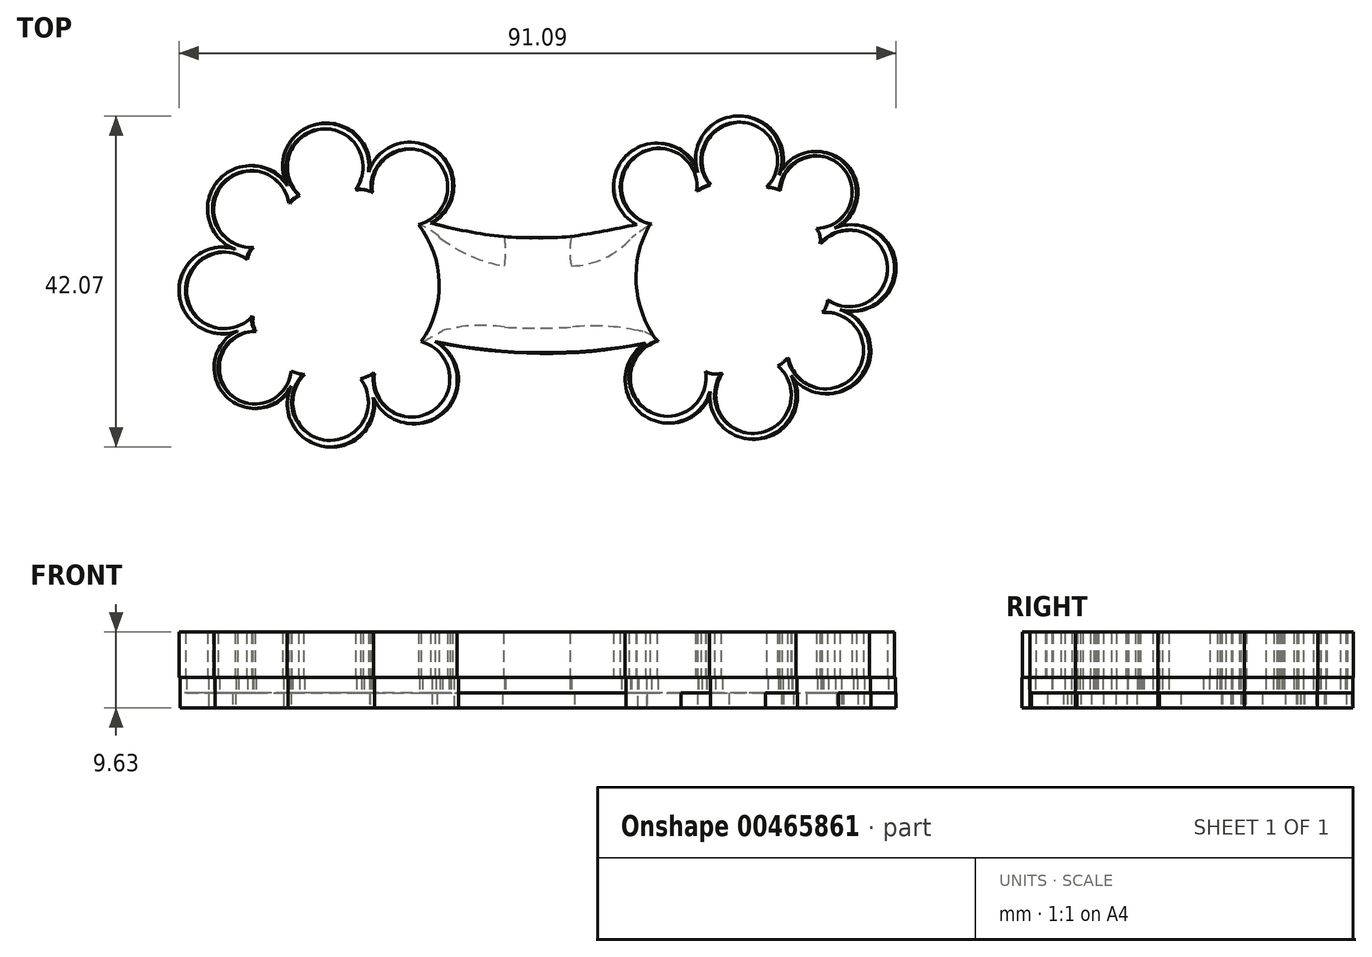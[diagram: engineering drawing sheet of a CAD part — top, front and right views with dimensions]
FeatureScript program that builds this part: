
annotation { "Feature Type Name" : "Feature", "Feature Type Description" : "" }
export const myFeature = defineFeature(function(context is Context, id is Id, definition is map)
    precondition{}
    {
        {
            var Q0;
            Q0=qCreatedBy(makeId("Top.planeOp"),FACE);
            var sketch = newSketch(context, id + "F0", { "sketchPlane" : qUnion([Q0])});
            skCircle(sketch, "E0", {"center": v(-25.13, 0.69) * mm, "radius": 13.9 * mm});
            skArc(sketch, "E1", {"start": v(-21.88, 14.2) * mm, "mid": v(-27.79, 21.36) * mm, "end": v(-31.7, 12.95) * mm});
            skArc(sketch, "E2", {"start": v(-31.7, 12.95) * mm, "mid": v(-40.8, 14.09) * mm, "end": v(-38.24, 5.29) * mm});
            skArc(sketch, "E3", {"start": v(-38.24, 5.29) * mm, "mid": v(-45.72, 0) * mm, "end": v(-37.92, -4.8) * mm});
            skArc(sketch, "E4", {"start": v(-13.74, 8.67) * mm, "mid": v(-13.36, 17.98) * mm, "end": v(-21.88, 14.2) * mm});
            skArc(sketch, "E5", {"start": v(-37.92, -4.8) * mm, "mid": v(-39.87, -13.17) * mm, "end": v(-31.4, -11.73) * mm});
            skArc(sketch, "E6", {"start": v(-31.4, -11.73) * mm, "mid": v(-27, -19.67) * mm, "end": v(-21.23, -12.67) * mm});
            skArc(sketch, "E7", {"start": v(-21.23, -12.67) * mm, "mid": v(-12.6, -15.51) * mm, "end": v(-13.19, -6.44) * mm});
            skCircle(sketch, "E8", {"center": v(24.65, 1.86) * mm, "radius": 13.9 * mm});
            skArc(sketch, "E9", {"start": v(21.94, -11.78) * mm, "mid": v(28.13, -18.69) * mm, "end": v(31.7, -10.13) * mm});
            skArc(sketch, "E10", {"start": v(31.7, -10.13) * mm, "mid": v(40.84, -10.9) * mm, "end": v(37.94, -2.21) * mm});
            skArc(sketch, "E11", {"start": v(37.94, -2.21) * mm, "mid": v(45.2, 3.37) * mm, "end": v(37.21, 7.85) * mm});
            skArc(sketch, "E12", {"start": v(13.6, -6.57) * mm, "mid": v(13.58, -15.89) * mm, "end": v(21.94, -11.78) * mm});
            skArc(sketch, "E13", {"start": v(37.21, 7.85) * mm, "mid": v(38.83, 16.3) * mm, "end": v(30.42, 14.52) * mm});
            skArc(sketch, "E14", {"start": v(30.42, 14.52) * mm, "mid": v(25.7, 22.28) * mm, "end": v(20.23, 15.05) * mm});
            skArc(sketch, "E15", {"start": v(20.23, 15.05) * mm, "mid": v(11.48, 17.55) * mm, "end": v(12.43, 8.5) * mm});
            skArc(sketch, "E16", {"start": v(-13.74, 8.67) * mm, "mid": v(-0.67, 6.75) * mm, "end": v(12.43, 8.5) * mm});
            skArc(sketch, "E17", {"start": v(-13.19, -6.44) * mm, "mid": v(0.2, -7.87) * mm, "end": v(13.6, -6.57) * mm});
            skSolve(sketch);
        }
        {
            var Q0;
            Q0=qCreatedBy(makeId("Top.planeOp"),FACE);
            var sketch = newSketch(context, id + "F1", { "sketchPlane" : qUnion([Q0])});
            skArc(sketch, "E18", {"start": v(-13.19, -6.4) * mm, "mid": v(0.16, -7.8) * mm, "end": v(13.53, -6.59) * mm});
            skArc(sketch, "E19", {"start": v(-13.74, 8.68) * mm, "mid": v(-9.16, 7.62) * mm, "end": v(-4.51, 6.92) * mm});
            skArc(sketch, "E20", {"start": v(3.97, 6.92) * mm, "mid": v(8.19, 7.63) * mm, "end": v(12.38, 8.49) * mm});
            skPoint(sketch, "E21.centerSnap0", {"position": v(38.52, 2.9) * mm});
            skArc(sketch, "E22", {"start": v(-21.88, 14.13) * mm, "mid": v(-27.8, 21.28) * mm, "end": v(-31.7, 12.87) * mm});
            skArc(sketch, "E23", {"start": v(-31.7, 12.87) * mm, "mid": v(-40.8, 14.01) * mm, "end": v(-38.25, 5.21) * mm});
            skArc(sketch, "E24", {"start": v(-38.25, 5.21) * mm, "mid": v(-45.73, -0.08) * mm, "end": v(-37.92, -4.87) * mm});
            skArc(sketch, "E25", {"start": v(-13.74, 8.68) * mm, "mid": v(-13.38, 18) * mm, "end": v(-21.88, 14.13) * mm});
            skArc(sketch, "E26", {"start": v(-37.92, -4.87) * mm, "mid": v(-39.87, -13.24) * mm, "end": v(-31.4, -11.8) * mm});
            skArc(sketch, "E27", {"start": v(-31.4, -11.8) * mm, "mid": v(-26.65, -19.77) * mm, "end": v(-21.48, -12.08) * mm});
            skArc(sketch, "E28", {"start": v(-21.48, -12.08) * mm, "mid": v(-12.8, -15.86) * mm, "end": v(-13.19, -6.4) * mm});
            skArc(sketch, "E29", {"start": v(21.88, -11.8) * mm, "mid": v(28.08, -18.7) * mm, "end": v(31.65, -10.14) * mm});
            skArc(sketch, "E30", {"start": v(31.65, -10.14) * mm, "mid": v(40.78, -10.92) * mm, "end": v(37.88, -2.23) * mm});
            skArc(sketch, "E31", {"start": v(37.88, -2.23) * mm, "mid": v(45.14, 3.36) * mm, "end": v(37.15, 7.83) * mm});
            skArc(sketch, "E32", {"start": v(13.53, -6.59) * mm, "mid": v(13.52, -15.9) * mm, "end": v(21.88, -11.8) * mm});
            skArc(sketch, "E33", {"start": v(37.15, 7.83) * mm, "mid": v(38.77, 16.28) * mm, "end": v(30.36, 14.5) * mm});
            skArc(sketch, "E34", {"start": v(30.36, 14.5) * mm, "mid": v(25.65, 22.26) * mm, "end": v(20.17, 15.03) * mm});
            skArc(sketch, "E35", {"start": v(20.17, 15.03) * mm, "mid": v(11.42, 17.53) * mm, "end": v(12.38, 8.49) * mm});
            skArc(sketch, "E36", {"start": v(-15.3, 8.48) * mm, "mid": v(-13.7, 17.23) * mm, "end": v(-21.3, 12.59) * mm});
            skArc(sketch, "E37", {"start": v(-23.3, 12.9) * mm, "mid": v(-27.7, 20.62) * mm, "end": v(-30.53, 12.19) * mm});
            skArc(sketch, "E38", {"start": v(-31.78, 11.18) * mm, "mid": v(-40.36, 13.54) * mm, "end": v(-36.4, 5.57) * mm});
            skArc(sketch, "E39", {"start": v(-37.13, 4.05) * mm, "mid": v(-44.87, -0.35) * mm, "end": v(-36.43, -3.18) * mm});
            skArc(sketch, "E40", {"start": v(-36.04, -5.08) * mm, "mid": v(-39.55, -12.8) * mm, "end": v(-31.5, -10.13) * mm});
            skArc(sketch, "E41", {"start": v(-29.91, -10.56) * mm, "mid": v(-26.92, -18.94) * mm, "end": v(-22.67, -11.12) * mm});
            skArc(sketch, "E42", {"start": v(-21.02, -10.4) * mm, "mid": v(-13.52, -15.18) * mm, "end": v(-14.95, -6.4) * mm});
            skArc(sketch, "E43", {"start": v(-12.69, 6.82) * mm, "mid": v(-8.83, 4.5) * mm, "end": v(-4.51, 3.24) * mm});
            skArc(sketch, "E44", {"start": v(-4.51, -4.53) * mm, "mid": v(-8.48, -4.33) * mm, "end": v(-12.4, -4.97) * mm});
            skArc(sketch, "E45", {"start": v(3.97, 3.24) * mm, "mid": v(8.16, 4.23) * mm, "end": v(11.6, 6.82) * mm});
            skArc(sketch, "E46", {"start": v(12.47, -4.97) * mm, "mid": v(8.24, -4.4) * mm, "end": v(3.97, -4.53) * mm});
            skArc(sketch, "E47", {"start": v(-12.69, 6.82) * mm, "mid": v(-13.9, 7.79) * mm, "end": v(-15.3, 8.48) * mm});
            skArc(sketch, "E48", {"start": v(-21.3, 12.59) * mm, "mid": v(-22.27, 12.92) * mm, "end": v(-23.3, 12.9) * mm});
            skArc(sketch, "E49", {"start": v(-30.53, 12.19) * mm, "mid": v(-31.21, 11.75) * mm, "end": v(-31.78, 11.18) * mm});
            skArc(sketch, "E50", {"start": v(-36.4, 5.57) * mm, "mid": v(-36.9, 4.88) * mm, "end": v(-37.13, 4.05) * mm});
            skArc(sketch, "E51", {"start": v(-36.43, -3.18) * mm, "mid": v(-36.45, -4.17) * mm, "end": v(-36.04, -5.08) * mm});
            skArc(sketch, "E52", {"start": v(-31.5, -10.13) * mm, "mid": v(-30.73, -10.41) * mm, "end": v(-29.91, -10.56) * mm});
            skArc(sketch, "E53", {"start": v(-22.67, -11.12) * mm, "mid": v(-21.81, -10.84) * mm, "end": v(-21.02, -10.4) * mm});
            skArc(sketch, "E54", {"start": v(-14.95, -6.4) * mm, "mid": v(-13.66, -5.7) * mm, "end": v(-12.4, -4.97) * mm});
            skArc(sketch, "E55", {"start": v(15, -6.32) * mm, "mid": v(13.72, -15.12) * mm, "end": v(21.14, -10.21) * mm});
            skArc(sketch, "E56", {"start": v(23.15, -10.44) * mm, "mid": v(27.82, -18.02) * mm, "end": v(30.35, -9.48) * mm});
            skArc(sketch, "E57", {"start": v(31.57, -8.44) * mm, "mid": v(40.23, -10.49) * mm, "end": v(35.98, -2.67) * mm});
            skArc(sketch, "E58", {"start": v(36.66, -1.12) * mm, "mid": v(44.23, 3.55) * mm, "end": v(35.7, 6.08) * mm});
            skArc(sketch, "E59", {"start": v(35.25, 7.97) * mm, "mid": v(38.48, 15.8) * mm, "end": v(30.54, 12.85) * mm});
            skArc(sketch, "E60", {"start": v(28.93, 13.22) * mm, "mid": v(25.64, 21.5) * mm, "end": v(21.67, 13.53) * mm});
            skArc(sketch, "E61", {"start": v(20.04, 12.75) * mm, "mid": v(12.38, 17.26) * mm, "end": v(14.12, 8.54) * mm});
            skArc(sketch, "E62", {"start": v(21.14, -10.21) * mm, "mid": v(22.12, -10.5) * mm, "end": v(23.15, -10.44) * mm});
            skArc(sketch, "E63", {"start": v(30.35, -9.48) * mm, "mid": v(31.02, -9.03) * mm, "end": v(31.57, -8.44) * mm});
            skArc(sketch, "E64", {"start": v(35.98, -2.67) * mm, "mid": v(36.47, -1.96) * mm, "end": v(36.66, -1.12) * mm});
            skArc(sketch, "E65", {"start": v(35.7, 6.08) * mm, "mid": v(35.68, 7.07) * mm, "end": v(35.25, 7.97) * mm});
            skArc(sketch, "E66", {"start": v(30.54, 12.85) * mm, "mid": v(29.75, 13.1) * mm, "end": v(28.93, 13.22) * mm});
            skArc(sketch, "E67", {"start": v(21.67, 13.53) * mm, "mid": v(20.82, 13.22) * mm, "end": v(20.04, 12.75) * mm});
            skArc(sketch, "E68", {"start": v(15, -6.32) * mm, "mid": v(13.88, -5.39) * mm, "end": v(12.47, -4.97) * mm});
            skArc(sketch, "E69", {"start": v(14.12, 8.54) * mm, "mid": v(12.83, 7.72) * mm, "end": v(11.6, 6.82) * mm});
            skArc(sketch, "E70", {"start": v(-4.51, -4.53) * mm, "mid": v(-0.27, -4.64) * mm, "end": v(3.97, -4.53) * mm});
            skArc(sketch, "E71", {"start": v(3.97, 6.92) * mm, "mid": v(3.78, 5.08) * mm, "end": v(3.97, 3.24) * mm});
            skArc(sketch, "E72", {"start": v(-4.51, 3.24) * mm, "mid": v(-4.39, 5.08) * mm, "end": v(-4.51, 6.92) * mm});
            skSolve(sketch);
        }
        {
            var Q0;
            Q0 = qSketchRegion(id + "F0", true);
            extrude(context, id + "F2", {"entities" : qUnion([Q0]), "depth" : 1.92 * mm});
        }
        {
            var Q0;
            Q0 = qSketchRegion(id + "F1", true);
            extrude(context, id + "F3", {"entities" : qUnion([Q0]), "operationType" : NewBodyOperationType.ADD, "depth" : 3.85 * mm});
        }
        {
            var Q0;
            Q0=makeQuery(id+"F3.opExtrude","CAP_FACE",FACE,{"disambiguationData":[OSD([sQuery(id+"F1.wireOp",EDGE,"E18"),sQuery(id+"F1.wireOp",EDGE,"E19"),sQuery(id+"F1.wireOp",EDGE,"E20"),sQuery(id+"F1.wireOp",EDGE,"E22"),sQuery(id+"F1.wireOp",EDGE,"E23"),sQuery(id+"F1.wireOp",EDGE,"E24"),sQuery(id+"F1.wireOp",EDGE,"E25"),sQuery(id+"F1.wireOp",EDGE,"E26"),sQuery(id+"F1.wireOp",EDGE,"E27"),sQuery(id+"F1.wireOp",EDGE,"E28"),sQuery(id+"F1.wireOp",EDGE,"E29"),sQuery(id+"F1.wireOp",EDGE,"E30"),sQuery(id+"F1.wireOp",EDGE,"E31"),sQuery(id+"F1.wireOp",EDGE,"E32"),sQuery(id+"F1.wireOp",EDGE,"E33"),sQuery(id+"F1.wireOp",EDGE,"E34"),sQuery(id+"F1.wireOp",EDGE,"E35"),sQuery(id+"F1.wireOp",EDGE,"E36"),sQuery(id+"F1.wireOp",EDGE,"E37"),sQuery(id+"F1.wireOp",EDGE,"E38"),sQuery(id+"F1.wireOp",EDGE,"E39"),sQuery(id+"F1.wireOp",EDGE,"E40"),sQuery(id+"F1.wireOp",EDGE,"E41"),sQuery(id+"F1.wireOp",EDGE,"E42"),sQuery(id+"F1.wireOp",EDGE,"E43"),sQuery(id+"F1.wireOp",EDGE,"E44"),sQuery(id+"F1.wireOp",EDGE,"E45"),sQuery(id+"F1.wireOp",EDGE,"E46"),sQuery(id+"F1.wireOp",EDGE,"E47"),sQuery(id+"F1.wireOp",EDGE,"E48"),sQuery(id+"F1.wireOp",EDGE,"E49"),sQuery(id+"F1.wireOp",EDGE,"E50"),sQuery(id+"F1.wireOp",EDGE,"E51"),sQuery(id+"F1.wireOp",EDGE,"E52"),sQuery(id+"F1.wireOp",EDGE,"E53"),sQuery(id+"F1.wireOp",EDGE,"E54"),sQuery(id+"F1.wireOp",EDGE,"E55"),sQuery(id+"F1.wireOp",EDGE,"E56"),sQuery(id+"F1.wireOp",EDGE,"E57"),sQuery(id+"F1.wireOp",EDGE,"E58"),sQuery(id+"F1.wireOp",EDGE,"E59"),sQuery(id+"F1.wireOp",EDGE,"E60"),sQuery(id+"F1.wireOp",EDGE,"E61"),sQuery(id+"F1.wireOp",EDGE,"E62"),sQuery(id+"F1.wireOp",EDGE,"E63"),sQuery(id+"F1.wireOp",EDGE,"E64"),sQuery(id+"F1.wireOp",EDGE,"E65"),sQuery(id+"F1.wireOp",EDGE,"E66"),sQuery(id+"F1.wireOp",EDGE,"E67"),sQuery(id+"F1.wireOp",EDGE,"E68"),sQuery(id+"F1.wireOp",EDGE,"E69"),sQuery(id+"F1.wireOp",EDGE,"E70"),sQuery(id+"F1.wireOp",EDGE,"E71"),sQuery(id+"F1.wireOp",EDGE,"E72")])],"isStart":false});
            var sketch = newSketch(context, id + "F4", { "sketchPlane" : qUnion([Q0])});
            skArc(sketch, "E73", {"start": v(-13.33, -6.37) * mm, "mid": v(0.02, -7.77) * mm, "end": v(13.4, -6.55) * mm});
            skArc(sketch, "E74", {"start": v(-13.88, 8.7) * mm, "mid": v(-9.3, 7.65) * mm, "end": v(-4.66, 6.96) * mm});
            skArc(sketch, "E75", {"start": v(3.83, 6.96) * mm, "mid": v(8.04, 7.67) * mm, "end": v(12.23, 8.52) * mm});
            skCircle(sketch, "E76", {"center": v(-25.27, 0.72) * mm, "radius": 0.22 * mm});
            skCircle(sketch, "E77", {"center": v(24.52, 1.87) * mm, "radius": 0.29 * mm});
            skArc(sketch, "E78", {"start": v(-22.02, 14.17) * mm, "mid": v(-27.93, 21.32) * mm, "end": v(-31.85, 12.9) * mm});
            skArc(sketch, "E79", {"start": v(-31.85, 12.9) * mm, "mid": v(-40.94, 14.05) * mm, "end": v(-38.4, 5.24) * mm});
            skArc(sketch, "E80", {"start": v(-38.4, 5.24) * mm, "mid": v(-45.87, -0.04) * mm, "end": v(-38.06, -4.83) * mm});
            skArc(sketch, "E81", {"start": v(-13.88, 8.7) * mm, "mid": v(-13.52, 18.04) * mm, "end": v(-22.02, 14.17) * mm});
            skArc(sketch, "E82", {"start": v(-38.06, -4.83) * mm, "mid": v(-40.02, -13.2) * mm, "end": v(-31.54, -11.78) * mm});
            skArc(sketch, "E83", {"start": v(-31.54, -11.78) * mm, "mid": v(-26.8, -19.73) * mm, "end": v(-21.62, -12.04) * mm});
            skArc(sketch, "E84", {"start": v(-21.62, -12.04) * mm, "mid": v(-12.95, -15.82) * mm, "end": v(-13.33, -6.37) * mm});
            skArc(sketch, "E85", {"start": v(21.74, -11.76) * mm, "mid": v(27.93, -18.67) * mm, "end": v(31.5, -10.1) * mm});
            skArc(sketch, "E86", {"start": v(31.5, -10.1) * mm, "mid": v(40.64, -10.89) * mm, "end": v(37.74, -2.2) * mm});
            skArc(sketch, "E87", {"start": v(37.74, -2.2) * mm, "mid": v(45, 3.39) * mm, "end": v(37, 7.86) * mm});
            skArc(sketch, "E88", {"start": v(13.4, -6.55) * mm, "mid": v(13.38, -15.87) * mm, "end": v(21.74, -11.76) * mm});
            skArc(sketch, "E89", {"start": v(37, 7.86) * mm, "mid": v(38.63, 16.3) * mm, "end": v(30.21, 14.54) * mm});
            skArc(sketch, "E90", {"start": v(30.21, 14.54) * mm, "mid": v(25.5, 22.3) * mm, "end": v(20.02, 15.06) * mm});
            skArc(sketch, "E91", {"start": v(20.02, 15.06) * mm, "mid": v(11.28, 17.56) * mm, "end": v(12.23, 8.52) * mm});
            skArc(sketch, "E92", {"start": v(-15.45, 8.51) * mm, "mid": v(-13.85, 17.26) * mm, "end": v(-21.44, 12.62) * mm});
            skArc(sketch, "E93", {"start": v(-23.45, 12.92) * mm, "mid": v(-27.85, 20.66) * mm, "end": v(-30.67, 12.22) * mm});
            skArc(sketch, "E94", {"start": v(-31.93, 11.22) * mm, "mid": v(-40.5, 13.57) * mm, "end": v(-36.54, 5.6) * mm});
            skArc(sketch, "E95", {"start": v(-37.28, 4.09) * mm, "mid": v(-45.01, -0.32) * mm, "end": v(-36.57, -3.14) * mm});
            skArc(sketch, "E96", {"start": v(-36.19, -5.05) * mm, "mid": v(-39.7, -12.76) * mm, "end": v(-31.65, -10.1) * mm});
            skArc(sketch, "E97", {"start": v(-30.06, -10.52) * mm, "mid": v(-27.07, -18.9) * mm, "end": v(-22.82, -11.08) * mm});
            skArc(sketch, "E98", {"start": v(-21.16, -10.36) * mm, "mid": v(-13.66, -15.15) * mm, "end": v(-15.1, -6.37) * mm});
            skArc(sketch, "E99", {"start": v(-21.44, 12.62) * mm, "mid": v(-22.42, 12.95) * mm, "end": v(-23.45, 12.92) * mm});
            skArc(sketch, "E100", {"start": v(-30.67, 12.22) * mm, "mid": v(-31.35, 11.79) * mm, "end": v(-31.93, 11.22) * mm});
            skArc(sketch, "E101", {"start": v(-36.54, 5.6) * mm, "mid": v(-37.05, 4.92) * mm, "end": v(-37.28, 4.09) * mm});
            skArc(sketch, "E102", {"start": v(-36.57, -3.14) * mm, "mid": v(-36.6, -4.14) * mm, "end": v(-36.19, -5.05) * mm});
            skArc(sketch, "E103", {"start": v(-31.65, -10.1) * mm, "mid": v(-30.87, -10.38) * mm, "end": v(-30.06, -10.52) * mm});
            skArc(sketch, "E104", {"start": v(-22.82, -11.08) * mm, "mid": v(-21.95, -10.8) * mm, "end": v(-21.16, -10.36) * mm});
            skArc(sketch, "E105", {"start": v(14.86, -6.28) * mm, "mid": v(13.57, -15.09) * mm, "end": v(21, -10.18) * mm});
            skArc(sketch, "E106", {"start": v(23, -10.41) * mm, "mid": v(27.68, -17.98) * mm, "end": v(30.2, -9.45) * mm});
            skArc(sketch, "E107", {"start": v(31.42, -8.4) * mm, "mid": v(40.08, -10.45) * mm, "end": v(35.84, -2.63) * mm});
            skArc(sketch, "E108", {"start": v(36.52, -1.09) * mm, "mid": v(44.1, 3.59) * mm, "end": v(35.56, 6.11) * mm});
            skArc(sketch, "E109", {"start": v(35.1, 8) * mm, "mid": v(38.34, 15.84) * mm, "end": v(30.4, 12.89) * mm});
            skArc(sketch, "E110", {"start": v(28.79, 13.26) * mm, "mid": v(25.5, 21.52) * mm, "end": v(21.53, 13.56) * mm});
            skArc(sketch, "E111", {"start": v(19.9, 12.78) * mm, "mid": v(12.23, 17.3) * mm, "end": v(13.98, 8.57) * mm});
            skArc(sketch, "E112", {"start": v(21, -10.18) * mm, "mid": v(21.98, -10.47) * mm, "end": v(23, -10.41) * mm});
            skArc(sketch, "E113", {"start": v(30.2, -9.45) * mm, "mid": v(30.87, -9) * mm, "end": v(31.42, -8.4) * mm});
            skArc(sketch, "E114", {"start": v(35.84, -2.63) * mm, "mid": v(36.32, -1.92) * mm, "end": v(36.52, -1.09) * mm});
            skArc(sketch, "E115", {"start": v(35.56, 6.11) * mm, "mid": v(35.54, 7.1) * mm, "end": v(35.1, 8) * mm});
            skArc(sketch, "E116", {"start": v(30.4, 12.89) * mm, "mid": v(29.6, 13.14) * mm, "end": v(28.79, 13.26) * mm});
            skArc(sketch, "E117", {"start": v(21.53, 13.56) * mm, "mid": v(20.68, 13.25) * mm, "end": v(19.9, 12.78) * mm});
            skArc(sketch, "E118", {"start": v(-4.66, 6.96) * mm, "mid": v(-0.41, 6.82) * mm, "end": v(3.83, 6.96) * mm});
            skArc(sketch, "E119", {"start": v(-15.1, -6.37) * mm, "mid": v(-12.81, 1.13) * mm, "end": v(-15.45, 8.51) * mm});
            skArc(sketch, "E120", {"start": v(13.98, 8.57) * mm, "mid": v(12.2, 1.01) * mm, "end": v(14.86, -6.28) * mm});
            skSolve(sketch);
        }
        {
            var Q0;
            Q0 = qSketchRegion(id + "F4", true);
            extrude(context, id + "F5", {"entities" : qUnion([Q0]), "operationType" : NewBodyOperationType.ADD, "depth" : 5.78 * mm});
        }
    });
